# Revit family: 3d0c3042-02c9-4433-823e-a8a08dd940e5
name_source: partatom
category: Windows
revit_build: Autodesk Revit 2014 (Build: 20130308_1515(x64)
units: mm (PartAtom-declared; Revit-internal decimal feet)

## types (3) — shared parameters
AAMA Designation = as Specified
Air Infiltration = as Specified
Analytic Construction = <None>
Description = Western Window Aluminum Awning Window - 670 Awning as Specified
Forced Entry Rating = as Specified
Frame Depth = 0' - 4 1/2"
Frame Design_Nail Fin = Yes
Frame Mounting Setback = 0' - 1"
Glazing Thickness = 0' - 0 7/8"
Heat Transfer Coefficient (U) = 1 BTU/(h·ft²·°F)
Keynote = as Specified
Manufacturer = Western Window Systems
Manufacturer Fax = 602-243-3119
Manufacturer Website = https://www.westernwindowsystems.com
Maximum Size = 42 - 120'' Width  ;  16 - 48'' Height
Meets Egress = as Specified
Miami Dade Conformance = as Specified
Model = 670 Awning
Operation = Awning Pair
Product Data = http://www.arcat.com
Product Properties = https://www.westernwindowsystems.com
R = 1.0000 (h·ft²·°F)/BTU
RO Spacing_Bottom = 0' - 0"
RO Spacing_Sides = 0' - 0 1/4"
RO Spacing_Top = 0' - 0 1/4"
Sales Information = https://www.westernwindowsystems.com
Standards Conformance = as Specified
Structural Test Pressure = as Specified
Thermal Resistance (R) = 1.0000 (h·ft²·°F)/BTU
U = 1 BTU/(h·ft²·°F)
URL = https://www.westernwindowsystems.com
Wall Closure = By host
Water Penetration = as Specified
zero-valued in all types: Expected Lifespan (Years), Maintenance Schedule (Months), SHGC, STC Rating, Solar Heat Gain Coefficient, VLT, Visual Light Transmittance, Warranty Duration (Years)

## per-type parameters (varying)
| type | Include Screen |
| Motorized | Yes |
| Push Out | No |
| Standard | Yes |

## geometry (parser evidence)
native form markers: Sweep x4
no freeform markers — native parametric forms only
